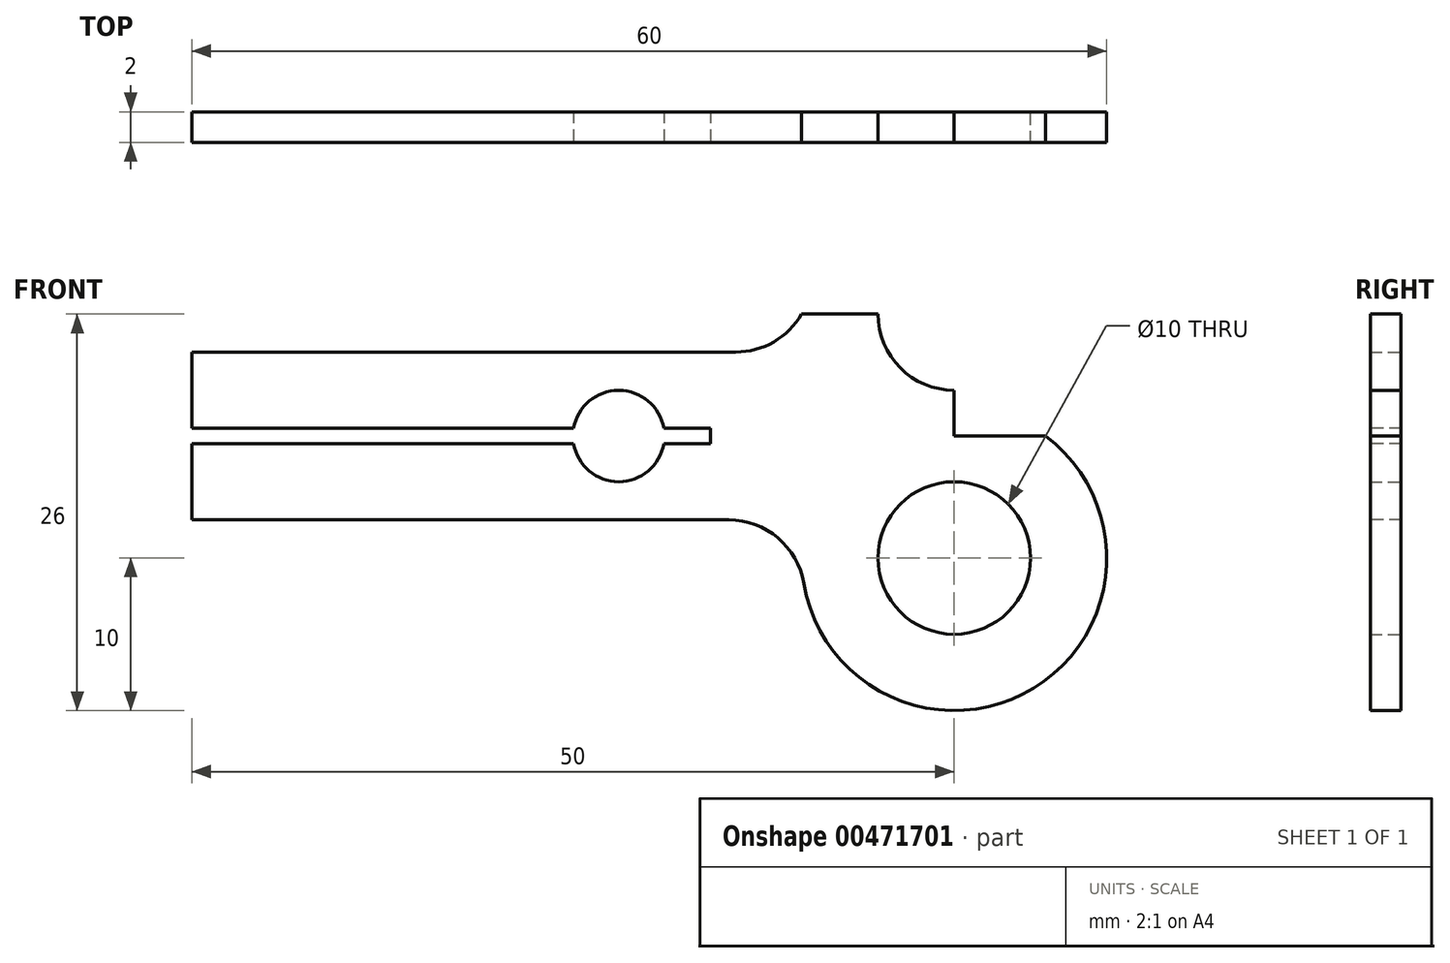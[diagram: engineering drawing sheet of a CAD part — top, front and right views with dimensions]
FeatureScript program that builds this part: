
annotation { "Feature Type Name" : "Feature", "Feature Type Description" : "" }
export const myFeature = defineFeature(function(context is Context, id is Id, definition is map)
    precondition{}
    {
        {
            var Q0;
            Q0=qCreatedBy(makeId("Front.planeOp"),FACE);
            var sketch = newSketch(context, id + "F0", { "sketchPlane" : qUnion([Q0])});
            skLineSegment(sketch, "E0.bottom", {"start": v(0, 0) * mm, "end": v(40, 0) * mm});
            skLineSegment(sketch, "E0.top", {"start": v(0, 11) * mm, "end": v(40, 11) * mm});
            skLineSegment(sketch, "E0.left", {"start": v(0, 0) * mm, "end": v(0, 11) * mm});
            skLineSegment(sketch, "E0.right", {"start": v(40, 0) * mm, "end": v(40, 11) * mm});
            skCircle(sketch, "E1", {"center": v(50, -2.5) * mm, "radius": 10 * mm});
            skCircle(sketch, "E2", {"center": v(50, 13.5) * mm, "radius": 10 * mm});
            skCircle(sketch, "E3", {"center": v(50, -2.5) * mm, "radius": 5 * mm});
            skCircle(sketch, "E4", {"center": v(50, 13.5) * mm, "radius": 5 * mm});
            skCircle(sketch, "E5", {"center": v(28, 5.5) * mm, "radius": 3 * mm});
            skPoint(sketch, "E5.centerSnap0", {"position": v(0, 5.5) * mm});
            skLineSegment(sketch, "E6", {"start": v(0, 5.5) * mm, "end": v(70.53, 5.5) * mm});
            skLineSegment(sketch, "E7.bottom", {"start": v(40, -2.5) * mm, "end": v(50, -2.5) * mm});
            skLineSegment(sketch, "E7.top", {"start": v(40, 13.5) * mm, "end": v(50, 13.5) * mm});
            skLineSegment(sketch, "E7.left", {"start": v(40, -2.5) * mm, "end": v(40, 13.5) * mm});
            skLineSegment(sketch, "E7.right", {"start": v(50, -2.5) * mm, "end": v(50, 13.5) * mm});
            skSolve(sketch);
        }
        {
            var Q0;
            Q0=makeQuery(id+"F0.imprint","IMPRINT",FACE,{"disambiguationData":[TD([[makeQuery(id+"F0.imprint","IMPRINT",EDGE,{"derivedFrom":sQuery(id+"F0.wireOp",EDGE,"E0.bottom")}),1.0]])]});
            var Q1;
            {var subQ0=sQuery(id+"F0.wireOp",EDGE,"E0.right");Q1=makeQuery(id+"F0.imprint","IMPRINT",FACE,{"disambiguationData":[TD([[makeQuery(id+"F0.imprint","IMPRINT",EDGE,{"derivedFrom":subQ0}),-1.0]])]});}
            var Q2;
            {var subQ0=sQuery(id+"F0.wireOp",EDGE,"E2");var subQ2=sQuery(id+"F0.wireOp",EDGE,"E1");var subQ3=makeQuery(id+"F0.imprint","INTERSECT",VERTEX,{"disambiguationData":[OD(0.0)],"derivedFrom":[subQ2,subQ0]});Q2=makeQuery(id+"F0.imprint","IMPRINT",FACE,{"disambiguationData":[TD([[makeQuery(id+"F0.imprint","IMPRINT",EDGE,{"disambiguationData":[TD([[subQ3,-1.0]])],"derivedFrom":subQ2}),-1.0]])]});}
            var Q3;
            {var subQ0=sQuery(id+"F0.wireOp",EDGE,"E2");var subQ1=sQuery(id+"F0.wireOp",EDGE,"E1");var subQ2=makeQuery(id+"F0.imprint","INTERSECT",VERTEX,{"disambiguationData":[OD(0.0)],"derivedFrom":[subQ1,subQ0]});Q3=makeQuery(id+"F0.imprint","IMPRINT",FACE,{"disambiguationData":[TD([[makeQuery(id+"F0.imprint","IMPRINT",EDGE,{"disambiguationData":[TD([[subQ2,-1.0]])],"derivedFrom":subQ1}),1.0]])]});}
            var Q4;
            {var subQ0=sQuery(id+"F0.wireOp",EDGE,"E2");var subQ1=sQuery(id+"F0.wireOp",EDGE,"E1");var subQ2=makeQuery(id+"F0.imprint","INTERSECT",VERTEX,{"disambiguationData":[OD(1.0)],"derivedFrom":[subQ1,subQ0]});Q4=makeQuery(id+"F0.imprint","IMPRINT",FACE,{"disambiguationData":[TD([[makeQuery(id+"F0.imprint","IMPRINT",EDGE,{"disambiguationData":[TD([[subQ2,-1.0]])],"derivedFrom":subQ0}),-1.0]])]});}
            var Q5;
            {var subQ5=sQuery(id+"F0.wireOp",EDGE,"E0.top");Q5=makeQuery(id+"F0.imprint","IMPRINT",FACE,{"disambiguationData":[TD([[makeQuery(id+"F0.imprint","IMPRINT",EDGE,{"derivedFrom":subQ5}),-1.0]])]});}
            var Q6;
            {var subQ0=sQuery(id+"F0.wireOp",EDGE,"E3");var subQ1=sQuery(id+"F0.wireOp",EDGE,"E2");var subQ2=makeQuery(id+"F0.imprint","INTERSECT",VERTEX,{"disambiguationData":[OD(0.0)],"derivedFrom":[subQ1,subQ0]});Q6=makeQuery(id+"F0.imprint","IMPRINT",FACE,{"disambiguationData":[TD([[makeQuery(id+"F0.imprint","IMPRINT",EDGE,{"disambiguationData":[TD([[subQ2,1.0]])],"derivedFrom":subQ0}),-1.0]])]});}
            var Q7;
            {var subQ0=sQuery(id+"F0.wireOp",EDGE,"E7.left");var subQ1=sQuery(id+"F0.wireOp",EDGE,"E7.top");var subQ2=makeQuery(id+"F0.imprint","INTERSECT",VERTEX,{"derivedFrom":[subQ1,subQ0]});Q7=makeQuery(id+"F0.imprint","IMPRINT",FACE,{"disambiguationData":[TD([[makeQuery(id+"F0.imprint","IMPRINT",EDGE,{"disambiguationData":[TD([[subQ2,-1.0]])],"derivedFrom":subQ1}),-1.0]])]});}
            var Q8;
            {var subQ0=sQuery(id+"F0.wireOp",EDGE,"E7.right");var subQ3=sQuery(id+"F0.wireOp",EDGE,"E6");var subQ5=makeQuery(id+"F0.imprint","INTERSECT",VERTEX,{"derivedFrom":[subQ3,subQ0]});Q8=makeQuery(id+"F0.imprint","IMPRINT",FACE,{"disambiguationData":[TD([[makeQuery(id+"F0.imprint","IMPRINT",EDGE,{"disambiguationData":[TD([[subQ5,1.0]])],"derivedFrom":subQ3}),1.0]])]});}
            var Q9;
            {var subQ0=sQuery(id+"F0.wireOp",EDGE,"E6");var subQ3=sQuery(id+"F0.wireOp",EDGE,"E7.right");var subQ5=makeQuery(id+"F0.imprint","INTERSECT",VERTEX,{"derivedFrom":[subQ0,subQ3]});Q9=makeQuery(id+"F0.imprint","IMPRINT",FACE,{"disambiguationData":[TD([[makeQuery(id+"F0.imprint","IMPRINT",EDGE,{"disambiguationData":[TD([[subQ5,1.0]])],"derivedFrom":subQ0}),-1.0]])]});}
            var Q10;
            {var subQ0=sQuery(id+"F0.wireOp",EDGE,"E7.left");var subQ1=sQuery(id+"F0.wireOp",EDGE,"E2");var subQ2=makeQuery(id+"F0.imprint","INTERSECT",VERTEX,{"derivedFrom":[subQ1,subQ0]});Q10=makeQuery(id+"F0.imprint","IMPRINT",FACE,{"disambiguationData":[TD([[makeQuery(id+"F0.imprint","IMPRINT",EDGE,{"disambiguationData":[TD([[subQ2,1.0]])],"derivedFrom":subQ0}),-1.0]])]});}
            var Q11;
            {var subQ1=sQuery(id+"F0.wireOp",EDGE,"E0.top");var subQ6=sQuery(id+"F0.wireOp",EDGE,"E0.left");var subQ11=makeQuery(id+"F0.imprint","INTERSECT",VERTEX,{"derivedFrom":[subQ1,subQ6]});Q11=makeQuery(id+"F0.imprint","IMPRINT",FACE,{"disambiguationData":[TD([[makeQuery(id+"F0.imprint","IMPRINT",EDGE,{"disambiguationData":[TD([[subQ11,-1.0]])],"derivedFrom":subQ1}),-1.0]])]});}
            var Q12;
            {var subQ5=sQuery(id+"F0.wireOp",EDGE,"E0.bottom");var subQ9=sQuery(id+"F0.wireOp",EDGE,"E0.left");var subQ10=makeQuery(id+"F0.imprint","INTERSECT",VERTEX,{"derivedFrom":[subQ5,subQ9]});Q12=makeQuery(id+"F0.imprint","IMPRINT",FACE,{"disambiguationData":[TD([[makeQuery(id+"F0.imprint","IMPRINT",EDGE,{"disambiguationData":[TD([[subQ10,-1.0]])],"derivedFrom":subQ5}),1.0]])]});}
            var Q13;
            {var subQ0=sQuery(id+"F0.wireOp",EDGE,"E6");var subQ3=sQuery(id+"F0.wireOp",EDGE,"E7.right");var subQ5=makeQuery(id+"F0.imprint","INTERSECT",VERTEX,{"derivedFrom":[subQ0,subQ3]});Q13=makeQuery(id+"F0.imprint","IMPRINT",FACE,{"disambiguationData":[TD([[makeQuery(id+"F0.imprint","IMPRINT",EDGE,{"disambiguationData":[TD([[subQ5,-1.0]])],"derivedFrom":subQ0}),-1.0]])]});}
            var Q14;
            {var subQ0=sQuery(id+"F0.wireOp",EDGE,"E7.left");var subQ1=sQuery(id+"F0.wireOp",EDGE,"E1");var subQ2=makeQuery(id+"F0.imprint","INTERSECT",VERTEX,{"derivedFrom":[subQ1,subQ0]});Q14=makeQuery(id+"F0.imprint","IMPRINT",FACE,{"disambiguationData":[TD([[makeQuery(id+"F0.imprint","IMPRINT",EDGE,{"disambiguationData":[TD([[subQ2,-1.0]])],"derivedFrom":subQ0}),-1.0]])]});}
            extrude(context, id + "F1", {"entities" : qUnion([Q0, Q1, Q2, Q3, Q4, Q5, Q6, Q7, Q8, Q9, Q10, Q11, Q12, Q13, Q14]), "depth" : 2 * mm, "offsetDistance" : 25 * mm});
        }
        {
            var Q0;
            Q0=makeQuery(id+"F1.opExtrude","SWEPT_EDGE",EDGE,{"disambiguationData":[OSD([sQuery(id+"F0.wireOp",EDGE,"E0.top"),sQuery(id+"F0.wireOp",EDGE,"E0.right"),sQuery(id+"F0.wireOp",EDGE,"E2")])]});
            var Q1;
            Q1=makeQuery(id+"F1.opExtrude","SWEPT_EDGE",EDGE,{"disambiguationData":[OSD([sQuery(id+"F0.wireOp",EDGE,"E0.bottom"),sQuery(id+"F0.wireOp",EDGE,"E0.right"),sQuery(id+"F0.wireOp",EDGE,"E1")])]});
            fillet(context, id + "F2", {"entities" : qUnion([Q0, Q1]), "radius" : 5 * mm, "tangentPropagation" : true, "allowEdgeOverflow" : false});
        }
        {
            var Q0;
            Q0=makeQuery(id+"F1.opExtrude","CAP_FACE",FACE,{"disambiguationData":[OSD([sQuery(id+"F0.wireOp",EDGE,"E0.bottom"),sQuery(id+"F0.wireOp",EDGE,"E0.top"),sQuery(id+"F0.wireOp",EDGE,"E0.left"),sQuery(id+"F0.wireOp",EDGE,"E1"),sQuery(id+"F0.wireOp",EDGE,"E2"),sQuery(id+"F0.wireOp",EDGE,"E3"),sQuery(id+"F0.wireOp",EDGE,"E4"),sQuery(id+"F0.wireOp",EDGE,"E5"),sQuery(id+"F0.wireOp",EDGE,"E7.left")])],"isStart":false});
            var sketch = newSketch(context, id + "F3", { "sketchPlane" : qUnion([Q0])});
            skLineSegment(sketch, "E8.bottom", {"start": v(0, 6) * mm, "end": v(34, 6) * mm});
            skLineSegment(sketch, "E9", {"start": v(0, 6) * mm, "end": v(0, 5) * mm});
            skLineSegment(sketch, "E10", {"start": v(0, 5) * mm, "end": v(34, 5) * mm});
            skLineSegment(sketch, "E11", {"start": v(34, 6) * mm, "end": v(34, 5) * mm});
            skSolve(sketch);
        }
        {
            var Q0;
            {var subQ0=sQuery(id+"F3.wireOp",EDGE,"E8.left");Q0=makeQuery(id+"F3.imprint","IMPRINT",FACE,{"disambiguationData":[TD([[makeQuery(id+"F3.imprint","IMPRINT",EDGE,{"derivedFrom":subQ0}),-1.0]])]});}
            var Q1;
            {var subQ0=sQuery(id+"F3.wireOp",EDGE,"E8.right");Q1=makeQuery(id+"F3.imprint","IMPRINT",FACE,{"disambiguationData":[TD([[makeQuery(id+"F3.imprint","IMPRINT",EDGE,{"derivedFrom":subQ0}),-1.0]])]});}
            var Q2;
            {var subQ0=sQuery(id+"F3.wireOp",EDGE,"E9");Q2=makeQuery(id+"F3.imprint","IMPRINT",FACE,{"disambiguationData":[TD([[makeQuery(id+"F3.imprint","IMPRINT",EDGE,{"derivedFrom":subQ0}),-1.0]])]});}
            var Q3;
            {var subQ0=sQuery(id+"F3.wireOp",EDGE,"E11");Q3=makeQuery(id+"F3.imprint","IMPRINT",FACE,{"disambiguationData":[TD([[makeQuery(id+"F3.imprint","IMPRINT",EDGE,{"derivedFrom":subQ0}),-1.0]])]});}
            extrude(context, id + "F4", {"entities" : qUnion([Q0, Q1, Q2, Q3]), "operationType" : NewBodyOperationType.REMOVE, "endBound" : BoundingType.UP_TO_NEXT, "oppositeDirection" : true, "depth" : 25 * mm});
        }
    });
